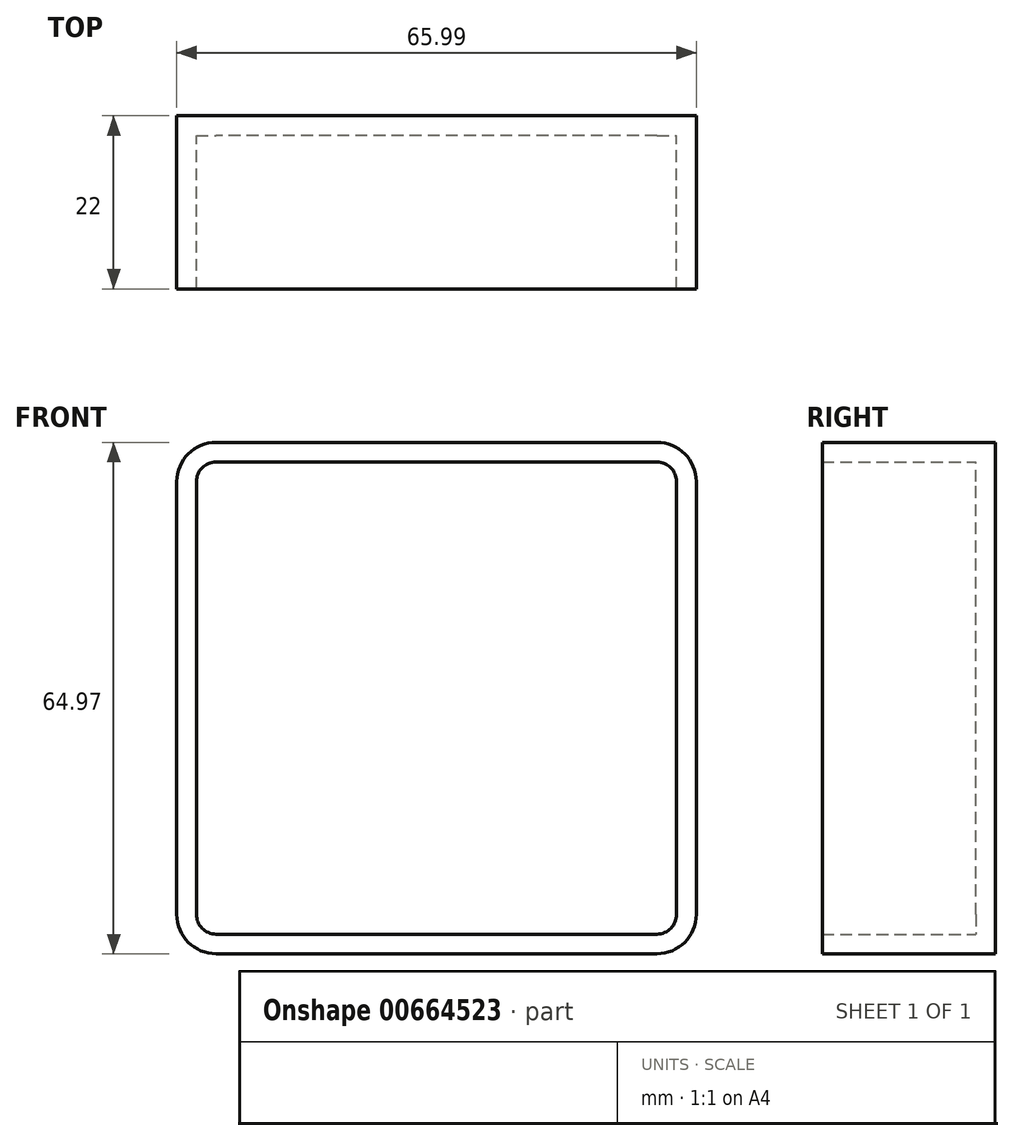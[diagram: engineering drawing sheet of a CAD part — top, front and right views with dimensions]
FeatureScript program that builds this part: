
annotation { "Feature Type Name" : "Feature", "Feature Type Description" : "" }
export const myFeature = defineFeature(function(context is Context, id is Id, definition is map)
    precondition{}
    {
        {
            var Q0;
            Q0=qCreatedBy(makeId("Front.planeOp"),FACE);
            var sketch = newSketch(context, id + "F0", { "sketchPlane" : qUnion([Q0])});
            skLineSegment(sketch, "E0.bottom", {"start": v(2.2, 0) * mm, "end": v(-63.8, 0) * mm});
            skLineSegment(sketch, "E0.top", {"start": v(2.2, 64.97) * mm, "end": v(-63.8, 64.97) * mm});
            skLineSegment(sketch, "E0.left", {"start": v(2.2, 0) * mm, "end": v(2.2, 64.97) * mm});
            skLineSegment(sketch, "E0.right", {"start": v(-63.8, 0) * mm, "end": v(-63.8, 64.97) * mm});
            skSolve(sketch);
        }
        {
            var Q0;
            Q0=makeQuery(id+"F0.imprint","IMPRINT",FACE,{"disambiguationData":[TD([[makeQuery(id+"F0.imprint","IMPRINT",EDGE,{"derivedFrom":sQuery(id+"F0.wireOp",EDGE,"E0.bottom")}),-1.0]])]});
            extrude(context, id + "F1", {"entities" : qUnion([Q0]), "depth" : 22 * mm, "offsetDistance" : 25.4 * mm});
        }
        {
            var Q0;
            Q0=makeQuery(id+"F1.opExtrude","SWEPT_EDGE",EDGE,{"disambiguationData":[OSD([sQuery(id+"F0.wireOp",EDGE,"E0.top"),sQuery(id+"F0.wireOp",EDGE,"E0.left")])]});
            var Q1;
            Q1=makeQuery(id+"F1.opExtrude","SWEPT_EDGE",EDGE,{"disambiguationData":[OSD([sQuery(id+"F0.wireOp",EDGE,"E0.bottom"),sQuery(id+"F0.wireOp",EDGE,"E0.left")])]});
            var Q2;
            Q2=makeQuery(id+"F1.opExtrude","SWEPT_EDGE",EDGE,{"disambiguationData":[OSD([sQuery(id+"F0.wireOp",EDGE,"E0.bottom"),sQuery(id+"F0.wireOp",EDGE,"E0.right")])]});
            var Q3;
            Q3=makeQuery(id+"F1.opExtrude","SWEPT_EDGE",EDGE,{"disambiguationData":[OSD([sQuery(id+"F0.wireOp",EDGE,"E0.top"),sQuery(id+"F0.wireOp",EDGE,"E0.right")])]});
            fillet(context, id + "F2", {"entities" : qUnion([Q0, Q1, Q2, Q3]), "radius" : 5 * mm, "tangentPropagation" : true, "allowEdgeOverflow" : false});
        }
        {
            var Q0;
            Q0=makeQuery(id+"F1.opExtrude","CAP_FACE",FACE,{"disambiguationData":[OSD([sQuery(id+"F0.wireOp",EDGE,"E0.bottom"),sQuery(id+"F0.wireOp",EDGE,"E0.top"),sQuery(id+"F0.wireOp",EDGE,"E0.left"),sQuery(id+"F0.wireOp",EDGE,"E0.right")])],"isStart":false});
            shell(context, id + "F3", {"entities" : qUnion([Q0]), "thickness" : 2.5 * mm});
        }
    });
